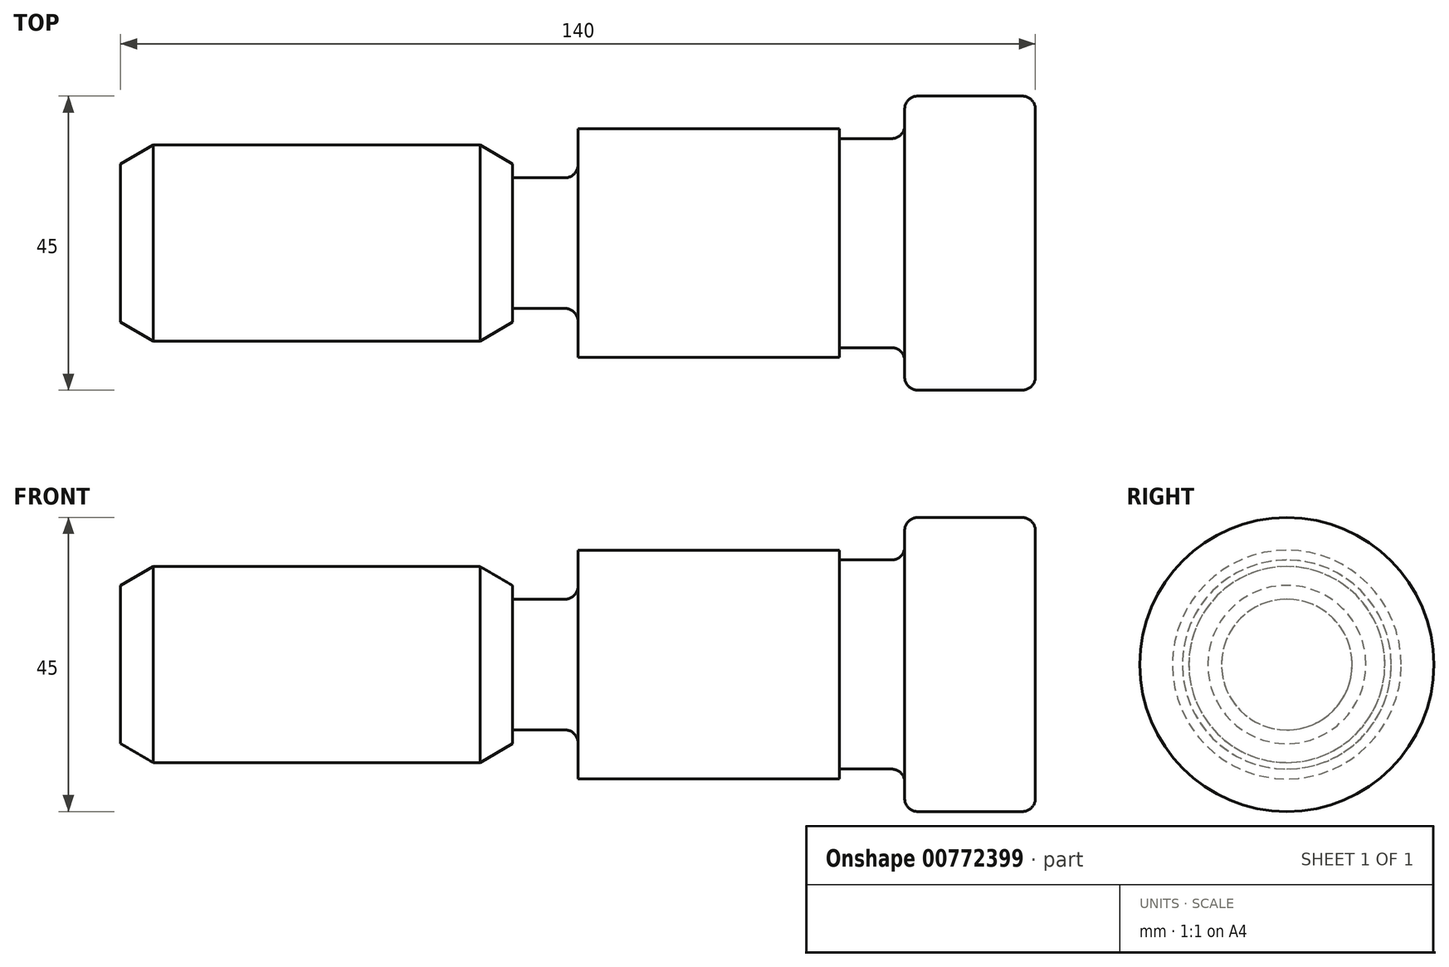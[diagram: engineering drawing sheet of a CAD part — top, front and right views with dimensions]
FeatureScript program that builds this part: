
annotation { "Feature Type Name" : "Feature", "Feature Type Description" : "" }
export const myFeature = defineFeature(function(context is Context, id is Id, definition is map)
    precondition{}
    {
        {
            var Q0;
            Q0=qCreatedBy(makeId("Front.planeOp"),FACE);
            var sketch = newSketch(context, id + "F0", { "sketchPlane" : qUnion([Q0])});
            skLineSegment(sketch, "E0", {"start": v(0, 0) * mm, "end": v(0, 22.5) * mm});
            skLineSegment(sketch, "E1", {"start": v(0, 22.5) * mm, "end": v(-20, 22.5) * mm});
            skLineSegment(sketch, "E2", {"start": v(-20, 22.5) * mm, "end": v(-20, 16) * mm});
            skLineSegment(sketch, "E3", {"start": v(-20, 16) * mm, "end": v(-30, 16) * mm});
            skLineSegment(sketch, "E4", {"start": v(-30, 16) * mm, "end": v(-30, 17.5) * mm});
            skLineSegment(sketch, "E5", {"start": v(-30, 17.5) * mm, "end": v(-70, 17.5) * mm});
            skLineSegment(sketch, "E6", {"start": v(-70, 17.5) * mm, "end": v(-70, 10) * mm});
            skLineSegment(sketch, "E7", {"start": v(-70, 10) * mm, "end": v(-80, 10) * mm});
            skLineSegment(sketch, "E8", {"start": v(-80, 10) * mm, "end": v(-80, 15) * mm});
            skLineSegment(sketch, "E9", {"start": v(-80, 15) * mm, "end": v(-140, 15) * mm});
            skLineSegment(sketch, "E10", {"start": v(-140, 15) * mm, "end": v(-140, 0) * mm});
            skLineSegment(sketch, "E11", {"start": v(-140, 0) * mm, "end": v(0, 0) * mm});
            skLineSegment(sketch, "E12", {"start": v(-96.8, 0) * mm, "end": v(-140, 0) * mm, "construction": true});
            skSolve(sketch);
        }
        {
            var Q0;
            Q0=makeQuery(id+"F0.imprint","IMPRINT",FACE,{"disambiguationData":[TD([[makeQuery(id+"F0.imprint","IMPRINT",EDGE,{"derivedFrom":sQuery(id+"F0.wireOp",EDGE,"E0")}),1.0]])]});
            var Q1;
            Q1=sQuery(id+"F0.wireOp",EDGE,"E11");
            revolve(context, id + "F1", {"surfaceOperationType" : NewSurfaceOperationType.NEW, "entities" : qUnion([Q0]), "axis" : qUnion([Q1]), "revolveType" : RevolveType.FULL});
        }
        {
            var Q0;
            Q0=makeQuery(id+"F1.opRevolve","SWEPT_EDGE",EDGE,{"disambiguationData":[OSD([sQuery(id+"F0.wireOp",EDGE,"E9"),sQuery(id+"F0.wireOp",EDGE,"E10")])]});
            var Q1;
            Q1=makeQuery(id+"F1.opRevolve","SWEPT_EDGE",EDGE,{"disambiguationData":[OSD([sQuery(id+"F0.wireOp",EDGE,"E8"),sQuery(id+"F0.wireOp",EDGE,"E9")])]});
            chamfer(context, id + "F2", {"entities" : qUnion([Q0, Q1]), "chamferType" : ChamferType.OFFSET_ANGLE, "width" : 5 * mm, "oppositeDirection" : true, "angle" : 30 * degree, "tangentPropagation" : true});
        }
        {
            var Q0;
            Q0=makeQuery(id+"F1.opRevolve","SWEPT_EDGE",EDGE,{"disambiguationData":[OSD([sQuery(id+"F0.wireOp",EDGE,"E6"),sQuery(id+"F0.wireOp",EDGE,"E7")])]});
            var Q1;
            Q1=makeQuery(id+"F1.opRevolve","SWEPT_EDGE",EDGE,{"disambiguationData":[OSD([sQuery(id+"F0.wireOp",EDGE,"E1"),sQuery(id+"F0.wireOp",EDGE,"E2")])]});
            var Q2;
            Q2=makeQuery(id+"F1.opRevolve","SWEPT_EDGE",EDGE,{"disambiguationData":[OSD([sQuery(id+"F0.wireOp",EDGE,"E0"),sQuery(id+"F0.wireOp",EDGE,"E1")])]});
            var Q3;
            Q3=makeQuery(id+"F1.opRevolve","SWEPT_EDGE",EDGE,{"disambiguationData":[OSD([sQuery(id+"F0.wireOp",EDGE,"E2"),sQuery(id+"F0.wireOp",EDGE,"E3")])]});
            fillet(context, id + "F3", {"entities" : qUnion([Q0, Q1, Q2, Q3]), "radius" : 2 * mm, "tangentPropagation" : true, "allowEdgeOverflow" : false});
        }
    });
